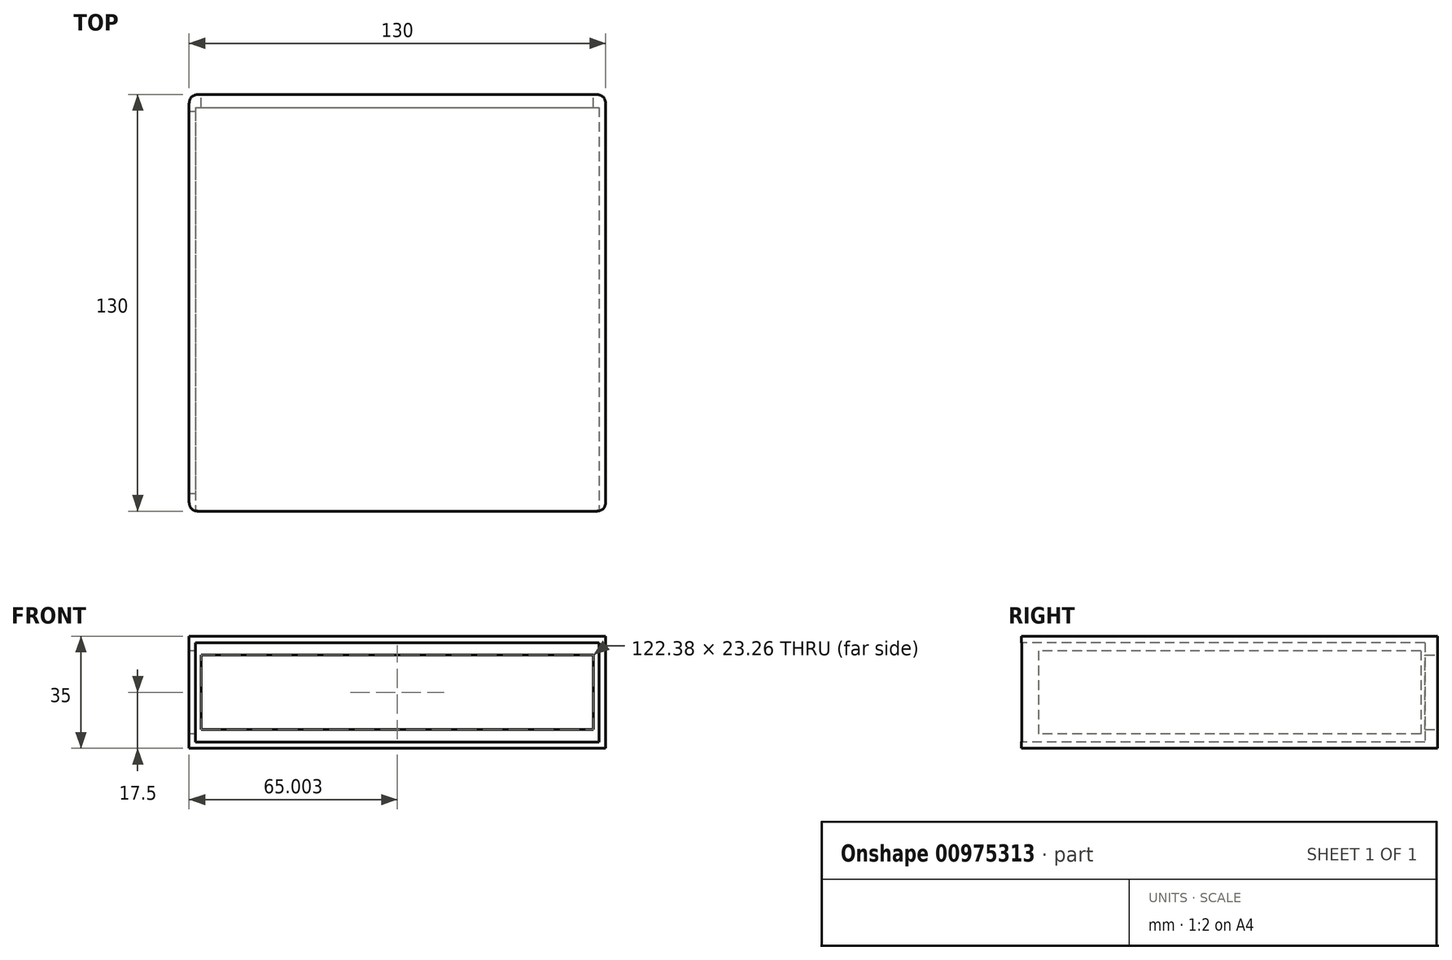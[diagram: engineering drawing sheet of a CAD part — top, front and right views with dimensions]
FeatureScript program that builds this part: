
annotation { "Feature Type Name" : "Feature", "Feature Type Description" : "" }
export const myFeature = defineFeature(function(context is Context, id is Id, definition is map)
    precondition{}
    {
        {
            var Q0;
            Q0=qCreatedBy(makeId("Top.planeOp"),FACE);
            var sketch = newSketch(context, id + "F0", { "sketchPlane" : qUnion([Q0])});
            skLineSegment(sketch, "E0.bottom", {"start": v(-63, 66.16) * mm, "end": v(67, 66.16) * mm});
            skLineSegment(sketch, "E0.top", {"start": v(-63, -63.84) * mm, "end": v(67, -63.84) * mm});
            skLineSegment(sketch, "E0.left", {"start": v(-63, 66.16) * mm, "end": v(-63, -63.84) * mm});
            skLineSegment(sketch, "E0.right", {"start": v(67, 66.16) * mm, "end": v(67, -63.84) * mm});
            skSolve(sketch);
        }
        {
            var Q0;
            Q0=makeQuery(id+"F0.imprint","IMPRINT",FACE,{"disambiguationData":[TD([[makeQuery(id+"F0.imprint","IMPRINT",EDGE,{"derivedFrom":sQuery(id+"F0.wireOp",EDGE,"E0.bottom")}),-1.0]])]});
            extrude(context, id + "F1", {"entities" : qUnion([Q0]), "endBound" : BoundingType.SYMMETRIC, "depth" : 35 * mm, "offsetDistance" : 25 * mm});
        }
        {
            var Q0;
            Q0=makeQuery(id+"F1.opExtrude","SWEPT_FACE",FACE,{"disambiguationData":[OSD([sQuery(id+"F0.wireOp",EDGE,"E0.top")])]});
            var sketch = newSketch(context, id + "F2", { "sketchPlane" : qUnion([Q0])});
            skLineSegment(sketch, "E1.bottom", {"start": v(-61, 15.5) * mm, "end": v(65, 15.5) * mm});
            skLineSegment(sketch, "E1.top", {"start": v(-61, -15.5) * mm, "end": v(65, -15.5) * mm});
            skLineSegment(sketch, "E1.left", {"start": v(-61, 15.5) * mm, "end": v(-61, -15.5) * mm});
            skLineSegment(sketch, "E1.right", {"start": v(65, 15.5) * mm, "end": v(65, -15.5) * mm});
            skSolve(sketch);
        }
        {
            var Q0;
            Q0=makeQuery(id+"F2.imprint","IMPRINT",FACE,{"disambiguationData":[TD([[makeQuery(id+"F2.imprint","IMPRINT",EDGE,{"derivedFrom":sQuery(id+"F2.wireOp",EDGE,"E1.bottom")}),-1.0]])]});
            extrude(context, id + "F3", {"entities" : qUnion([Q0]), "operationType" : NewBodyOperationType.REMOVE, "oppositeDirection" : true, "depth" : 126 * mm, "offsetDistance" : 25 * mm});
        }
        {
            var Q0;
            Q0=makeQuery(id+"F1.opExtrude","SWEPT_FACE",FACE,{"disambiguationData":[OSD([sQuery(id+"F0.wireOp",EDGE,"E0.left")])]});
            var sketch = newSketch(context, id + "F4", { "sketchPlane" : qUnion([Q0])});
            skLineSegment(sketch, "E2.bottom", {"start": v(-60.85, 12.94) * mm, "end": v(58.42, 12.94) * mm});
            skLineSegment(sketch, "E2.top", {"start": v(-60.85, -13.06) * mm, "end": v(58.42, -13.06) * mm});
            skLineSegment(sketch, "E2.left", {"start": v(-60.85, 12.94) * mm, "end": v(-60.85, -13.06) * mm});
            skLineSegment(sketch, "E2.right", {"start": v(58.42, 12.94) * mm, "end": v(58.42, -13.06) * mm});
            skSolve(sketch);
        }
        {
            var Q0;
            Q0=makeQuery(id+"F1.opExtrude","SWEPT_FACE",FACE,{"disambiguationData":[OSD([sQuery(id+"F0.wireOp",EDGE,"E0.bottom")])]});
            var sketch = newSketch(context, id + "F5", { "sketchPlane" : qUnion([Q0])});
            skLineSegment(sketch, "E3.bottom", {"start": v(-63.2, 11.63) * mm, "end": v(59.19, 11.63) * mm});
            skLineSegment(sketch, "E3.top", {"start": v(-63.2, -11.63) * mm, "end": v(59.19, -11.63) * mm});
            skLineSegment(sketch, "E3.left", {"start": v(-63.2, 11.63) * mm, "end": v(-63.2, -11.63) * mm});
            skLineSegment(sketch, "E3.right", {"start": v(59.19, 11.63) * mm, "end": v(59.19, -11.63) * mm});
            skSolve(sketch);
        }
        {
            var Q0;
            Q0=makeQuery(id+"F5.imprint","IMPRINT",FACE,{"disambiguationData":[TD([[makeQuery(id+"F5.imprint","IMPRINT",EDGE,{"derivedFrom":sQuery(id+"F5.wireOp",EDGE,"E3.bottom")}),-1.0]])]});
            extrude(context, id + "F6", {"entities" : qUnion([Q0]), "operationType" : NewBodyOperationType.REMOVE, "oppositeDirection" : true, "depth" : 7 * mm, "offsetDistance" : 25 * mm});
        }
        {
            var Q0;
            Q0=makeQuery(id+"F4.imprint","IMPRINT",FACE,{"disambiguationData":[TD([[makeQuery(id+"F4.imprint","IMPRINT",EDGE,{"derivedFrom":sQuery(id+"F4.wireOp",EDGE,"E2.bottom")}),-1.0]])]});
            extrude(context, id + "F7", {"entities" : qUnion([Q0]), "operationType" : NewBodyOperationType.REMOVE, "oppositeDirection" : true, "depth" : 3 * mm, "offsetDistance" : 25 * mm});
        }
        {
            var Q0;
            Q0=makeQuery(id+"F1.opExtrude","SWEPT_EDGE",EDGE,{"disambiguationData":[OSD([sQuery(id+"F0.wireOp",EDGE,"E0.bottom"),sQuery(id+"F0.wireOp",EDGE,"E0.left")])]});
            var Q1;
            Q1=makeQuery(id+"F1.opExtrude","SWEPT_EDGE",EDGE,{"disambiguationData":[OSD([sQuery(id+"F0.wireOp",EDGE,"E0.top"),sQuery(id+"F0.wireOp",EDGE,"E0.left")])]});
            var Q2;
            Q2=makeQuery(id+"F1.opExtrude","SWEPT_EDGE",EDGE,{"disambiguationData":[OSD([sQuery(id+"F0.wireOp",EDGE,"E0.bottom"),sQuery(id+"F0.wireOp",EDGE,"E0.right")])]});
            var Q3;
            Q3=makeQuery(id+"F1.opExtrude","SWEPT_EDGE",EDGE,{"disambiguationData":[OSD([sQuery(id+"F0.wireOp",EDGE,"E0.top"),sQuery(id+"F0.wireOp",EDGE,"E0.right")])]});
            fillet(context, id + "F8", {"entities" : qUnion([Q0, Q1, Q2, Q3]), "radius" : 3 * mm, "tangentPropagation" : true, "rho" : 0.5, "crossSection" : FilletCrossSection.CONIC, "allowEdgeOverflow" : false});
        }
    });
